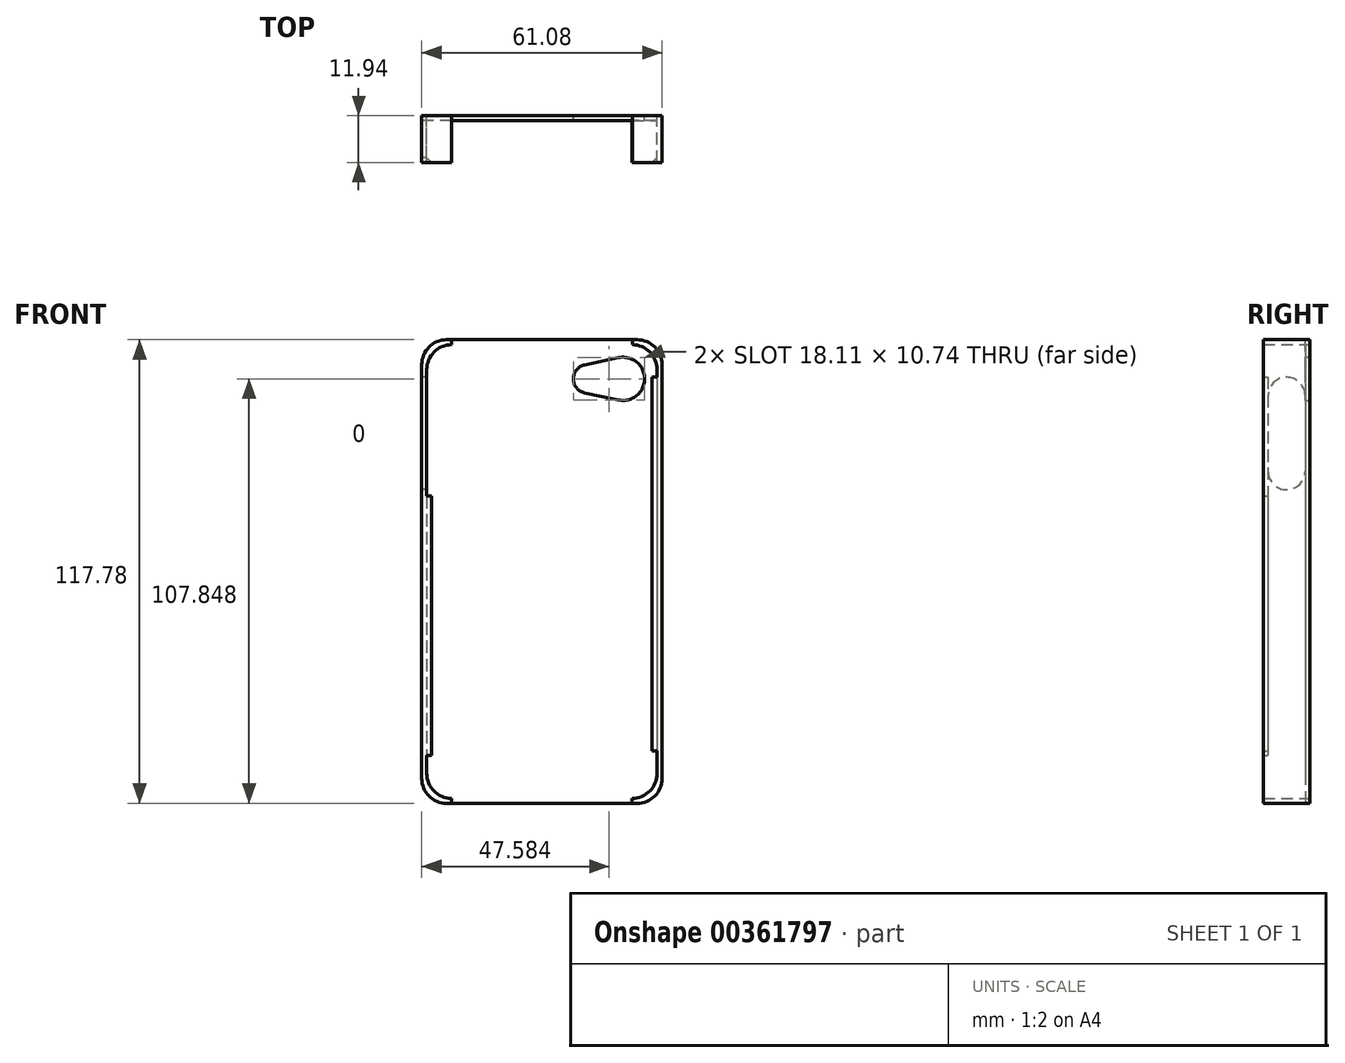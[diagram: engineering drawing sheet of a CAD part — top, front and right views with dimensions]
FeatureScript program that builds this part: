
annotation { "Feature Type Name" : "Feature", "Feature Type Description" : "" }
export const myFeature = defineFeature(function(context is Context, id is Id, definition is map)
    precondition{}
    {
        {
            var Q0;
            Q0=qCreatedBy(makeId("Front.planeOp"),FACE);
            var sketch = newSketch(context, id + "F0", { "sketchPlane" : qUnion([Q0])});
            skLineSegment(sketch, "E0.left", {"start": v(-75.12, 56.4) * mm, "end": v(-75.12, -46.14) * mm});
            skLineSegment(sketch, "E0.right", {"start": v(-16.58, 56.4) * mm, "end": v(-16.58, -46.14) * mm});
            skPoint(sketch, "E1.visualSharp", {"position": v(-16.58, 62.75) * mm});
            skArc(sketch, "E1.filletArc", {"start": v(-16.58, 56.4) * mm, "mid": v(-18.43, 60.88) * mm, "end": v(-22.9, 62.75) * mm});
            skPoint(sketch, "E2.visualSharp", {"position": v(-75.12, 62.75) * mm});
            skArc(sketch, "E2.filletArc", {"start": v(-68.77, 62.75) * mm, "mid": v(-73.26, 60.89) * mm, "end": v(-75.12, 56.4) * mm});
            skPoint(sketch, "E3.visualSharp", {"position": v(-75.12, -52.5) * mm});
            skArc(sketch, "E3.filletArc", {"start": v(-75.12, -46.14) * mm, "mid": v(-73.26, -50.63) * mm, "end": v(-68.77, -52.5) * mm});
            skPoint(sketch, "E4.visualSharp", {"position": v(-16.58, -52.5) * mm});
            skArc(sketch, "E4.filletArc", {"start": v(-22.93, -52.5) * mm, "mid": v(-18.44, -50.63) * mm, "end": v(-16.58, -46.14) * mm});
            skLineSegment(sketch, "E5.bottom", {"start": v(-70.04, 64.02) * mm, "end": v(-68.77, 64.02) * mm});
            skLineSegment(sketch, "E5.top", {"start": v(-70.04, -53.76) * mm, "end": v(-68.77, -53.76) * mm});
            skLineSegment(sketch, "E5.left", {"start": v(-76.4, 57.67) * mm, "end": v(-76.4, -47.41) * mm});
            skLineSegment(sketch, "E5.right", {"start": v(-15.3, 57.67) * mm, "end": v(-15.3, -47.41) * mm});
            skPoint(sketch, "E6.visualSharp", {"position": v(-15.3, 64.02) * mm});
            skArc(sketch, "E6.filletArc", {"start": v(-15.3, 57.67) * mm, "mid": v(-17.17, 62.16) * mm, "end": v(-21.66, 64.02) * mm});
            skPoint(sketch, "E7.visualSharp", {"position": v(-76.4, 64.02) * mm});
            skArc(sketch, "E7.filletArc", {"start": v(-70.04, 64.02) * mm, "mid": v(-74.53, 62.16) * mm, "end": v(-76.4, 57.67) * mm});
            skPoint(sketch, "E8.visualSharp", {"position": v(-76.4, -53.76) * mm});
            skArc(sketch, "E8.filletArc", {"start": v(-76.4, -47.41) * mm, "mid": v(-74.53, -51.9) * mm, "end": v(-70.04, -53.76) * mm});
            skPoint(sketch, "E9.visualSharp", {"position": v(-15.3, -53.76) * mm});
            skArc(sketch, "E9.filletArc", {"start": v(-21.66, -53.76) * mm, "mid": v(-17.17, -51.9) * mm, "end": v(-15.3, -47.41) * mm});
            skLineSegment(sketch, "E10", {"start": v(-68.77, -52.5) * mm, "end": v(-68.77, -53.76) * mm});
            skLineSegment(sketch, "E11", {"start": v(-22.93, -52.5) * mm, "end": v(-22.93, -53.76) * mm});
            skLineSegment(sketch, "E12.trimOffspring", {"start": v(-22.93, -53.76) * mm, "end": v(-21.66, -53.76) * mm});
            skLineSegment(sketch, "E13", {"start": v(-68.77, 62.75) * mm, "end": v(-68.77, 64.02) * mm});
            skLineSegment(sketch, "E14", {"start": v(-22.9, 62.75) * mm, "end": v(-22.9, 64.02) * mm});
            skLineSegment(sketch, "E15.trimOffspring", {"start": v(-22.9, 64.02) * mm, "end": v(-21.66, 64.02) * mm});
            skLineSegment(sketch, "E16", {"start": v(-68.77, 64.02) * mm, "end": v(-22.9, 64.02) * mm});
            skLineSegment(sketch, "E17", {"start": v(-68.77, -53.76) * mm, "end": v(-22.93, -53.76) * mm});
            skCircle(sketch, "E18", {"center": v(-25.24, 54.09) * mm, "radius": 5.48 * mm});
            skCircle(sketch, "E19", {"center": v(-34.23, 54.09) * mm, "radius": 3.64 * mm});
            skLineSegment(sketch, "E20", {"start": v(-26.36, 59.46) * mm, "end": v(-34.97, 57.65) * mm});
            skLineSegment(sketch, "E21", {"start": v(-26.36, 48.72) * mm, "end": v(-34.97, 50.53) * mm});
            skSolve(sketch);
        }
        {
            var Q0;
            Q0=makeQuery(id+"F0.imprint","IMPRINT",FACE,{"disambiguationData":[TD([[makeQuery(id+"F0.imprint","IMPRINT",EDGE,{"derivedFrom":sQuery(id+"F0.wireOp",EDGE,"E0.left")}),1.0]])]});
            extrude(context, id + "F1", {"entities" : qUnion([Q0]), "depth" : 1.27 * mm});
        }
        {
            var Q0;
            Q0=makeQuery(id+"F0.imprint","IMPRINT",FACE,{"disambiguationData":[TD([[makeQuery(id+"F0.imprint","IMPRINT",EDGE,{"derivedFrom":sQuery(id+"F0.wireOp",EDGE,"E0.left")}),-1.0]])]});
            var Q1;
            Q1=makeQuery(id+"F0.imprint","IMPRINT",FACE,{"disambiguationData":[TD([[makeQuery(id+"F0.imprint","IMPRINT",EDGE,{"derivedFrom":sQuery(id+"F0.wireOp",EDGE,"E0.right")}),1.0]])]});
            extrude(context, id + "F2", {"entities" : qUnion([Q0, Q1]), "operationType" : NewBodyOperationType.ADD, "depth" : 11.94 * mm});
        }
        {
            var Q0;
            Q0=makeQuery(id+"F2.opExtrude","SWEPT_FACE",FACE,{"disambiguationData":[OSD([sQuery(id+"F0.wireOp",EDGE,"E5.left")])]});
            var sketch = newSketch(context, id + "F3", { "sketchPlane" : qUnion([Q0])});
            skCircle(sketch, "E22", {"center": v(5.97, 49.8) * mm, "radius": 4.7 * mm});
            skCircle(sketch, "E23", {"center": v(5.97, 30.62) * mm, "radius": 4.7 * mm});
            skLineSegment(sketch, "E24", {"start": v(1.27, 49.8) * mm, "end": v(1.27, 30.62) * mm});
            skLineSegment(sketch, "E25", {"start": v(10.67, 30.62) * mm, "end": v(10.67, 49.8) * mm});
            skSolve(sketch);
        }
        {
            var Q0;
            {var subQ0=sQuery(id+"F3.wireOp",EDGE,"E24");Q0=makeQuery(id+"F3.imprint","IMPRINT",FACE,{"disambiguationData":[TD([[makeQuery(id+"F3.imprint","IMPRINT",EDGE,{"derivedFrom":subQ0}),1.0]])]});}
            var Q1;
            {var subQ0=sQuery(id+"F3.wireOp",EDGE,"E22");var subQ1=makeQuery(id+"F3.imprint","INTERSECT",VERTEX,{"derivedFrom":[subQ0,sQuery(id+"F3.wireOp",EDGE,"E24")]});Q1=makeQuery(id+"F3.imprint","IMPRINT",FACE,{"disambiguationData":[TD([[makeQuery(id+"F3.imprint","IMPRINT",EDGE,{"disambiguationData":[TD([[subQ1,1.0]])],"derivedFrom":subQ0}),1.0]])]});}
            var Q2;
            {var subQ0=sQuery(id+"F3.wireOp",EDGE,"E23");var subQ1=makeQuery(id+"F3.imprint","INTERSECT",VERTEX,{"derivedFrom":[subQ0,sQuery(id+"F3.wireOp",EDGE,"E24")]});Q2=makeQuery(id+"F3.imprint","IMPRINT",FACE,{"disambiguationData":[TD([[makeQuery(id+"F3.imprint","IMPRINT",EDGE,{"disambiguationData":[TD([[subQ1,1.0]])],"derivedFrom":subQ0}),1.0]])]});}
            extrude(context, id + "F4", {"entities" : qUnion([Q0, Q1, Q2]), "operationType" : NewBodyOperationType.REMOVE, "oppositeDirection" : true, "depth" : 25.4 * mm});
        }
        {
            var Q0;
            Q0=makeQuery(id+"F0.imprint","IMPRINT",FACE,{"disambiguationData":[TD([[makeQuery(id+"F0.imprint","IMPRINT",EDGE,{"derivedFrom":sQuery(id+"F0.wireOp",EDGE,"E0.right")}),-1.0]])]});
            extrude(context, id + "F5", {"entities" : qUnion([Q0]), "depth" : 1.27 * mm});
        }
        {
            var Q0;
            Q0=makeQuery(id+"F2.opExtrude","SWEPT_FACE",FACE,{"disambiguationData":[OSD([sQuery(id+"F0.wireOp",EDGE,"E0.left")])]});
            var sketch = newSketch(context, id + "F6", { "sketchPlane" : qUnion([Q0])});
            skLineSegment(sketch, "E26.bottom", {"start": v(-11.94, 24.38) * mm, "end": v(-10.67, 24.38) * mm});
            skLineSegment(sketch, "E26.top", {"start": v(-11.94, -41.62) * mm, "end": v(-10.67, -41.62) * mm});
            skLineSegment(sketch, "E26.left", {"start": v(-11.94, 24.38) * mm, "end": v(-11.94, -41.62) * mm});
            skLineSegment(sketch, "E26.right", {"start": v(-10.67, 24.38) * mm, "end": v(-10.67, -41.62) * mm});
            skSolve(sketch);
        }
        {
            var Q0;
            Q0=makeQuery(id+"F6.imprint","IMPRINT",FACE,{"disambiguationData":[TD([[makeQuery(id+"F6.imprint","IMPRINT",EDGE,{"derivedFrom":sQuery(id+"F6.wireOp",EDGE,"E26.bottom")}),-1.0]])]});
            extrude(context, id + "F7", {"entities" : qUnion([Q0]), "operationType" : NewBodyOperationType.ADD, "depth" : 1.27 * mm});
        }
        {
            var Q0;
            Q0=makeQuery(id+"F2.opExtrude","SWEPT_FACE",FACE,{"disambiguationData":[OSD([sQuery(id+"F0.wireOp",EDGE,"E0.right")])]});
            var sketch = newSketch(context, id + "F8", { "sketchPlane" : qUnion([Q0])});
            skLineSegment(sketch, "E27.bottom", {"start": v(11.94, 54.52) * mm, "end": v(10.67, 54.52) * mm});
            skLineSegment(sketch, "E27.top", {"start": v(11.94, -40.48) * mm, "end": v(10.67, -40.48) * mm});
            skLineSegment(sketch, "E27.left", {"start": v(11.94, 54.52) * mm, "end": v(11.94, -40.48) * mm});
            skLineSegment(sketch, "E27.right", {"start": v(10.67, 54.52) * mm, "end": v(10.67, -40.48) * mm});
            skSolve(sketch);
        }
        {
            var Q0;
            Q0=makeQuery(id+"F8.imprint","IMPRINT",FACE,{"disambiguationData":[TD([[makeQuery(id+"F8.imprint","IMPRINT",EDGE,{"derivedFrom":sQuery(id+"F8.wireOp",EDGE,"E27.bottom")}),1.0]])]});
            extrude(context, id + "F9", {"entities" : qUnion([Q0]), "operationType" : NewBodyOperationType.ADD, "depth" : 1.27 * mm});
        }
        {
            var Q0;
            Q0=makeQuery(id+"F9.opExtrude","SWEPT_FACE",FACE,{"disambiguationData":[OSD([sQuery(id+"F8.wireOp",EDGE,"E27.bottom")])]});
            var sketch = newSketch(context, id + "F10", { "sketchPlane" : qUnion([Q0])});
            skLineSegment(sketch, "E28", {"start": v(-16.58, -10.67) * mm, "end": v(-17.85, -11.94) * mm});
            skSolve(sketch);
        }
        {
            var Q0;
            Q0=makeQuery(id+"F10.imprint","IMPRINT",FACE,{"disambiguationData":[TD([[makeQuery(id+"F10.imprint","IMPRINT",EDGE,{"derivedFrom":sQuery(id+"F10.wireOp",EDGE,"E28")}),-1.0]])]});
            extrude(context, id + "F11", {"entities" : qUnion([Q0]), "operationType" : NewBodyOperationType.REMOVE, "oppositeDirection" : true, "depth" : 95 * mm});
        }
        {
            var Q0;
            Q0=makeQuery(id+"F7.opExtrude","SWEPT_FACE",FACE,{"disambiguationData":[OSD([sQuery(id+"F6.wireOp",EDGE,"E26.bottom")])]});
            var sketch = newSketch(context, id + "F12", { "sketchPlane" : qUnion([Q0])});
            skLineSegment(sketch, "E29", {"start": v(-75.12, -10.67) * mm, "end": v(-73.85, -11.94) * mm});
            skSolve(sketch);
        }
        {
            var Q0;
            Q0=makeQuery(id+"F12.imprint","IMPRINT",FACE,{"disambiguationData":[TD([[makeQuery(id+"F12.imprint","IMPRINT",EDGE,{"derivedFrom":sQuery(id+"F12.wireOp",EDGE,"E29")}),1.0]])]});
            extrude(context, id + "F13", {"entities" : qUnion([Q0]), "operationType" : NewBodyOperationType.REMOVE, "oppositeDirection" : true, "depth" : 68.58 * mm});
        }
    });
